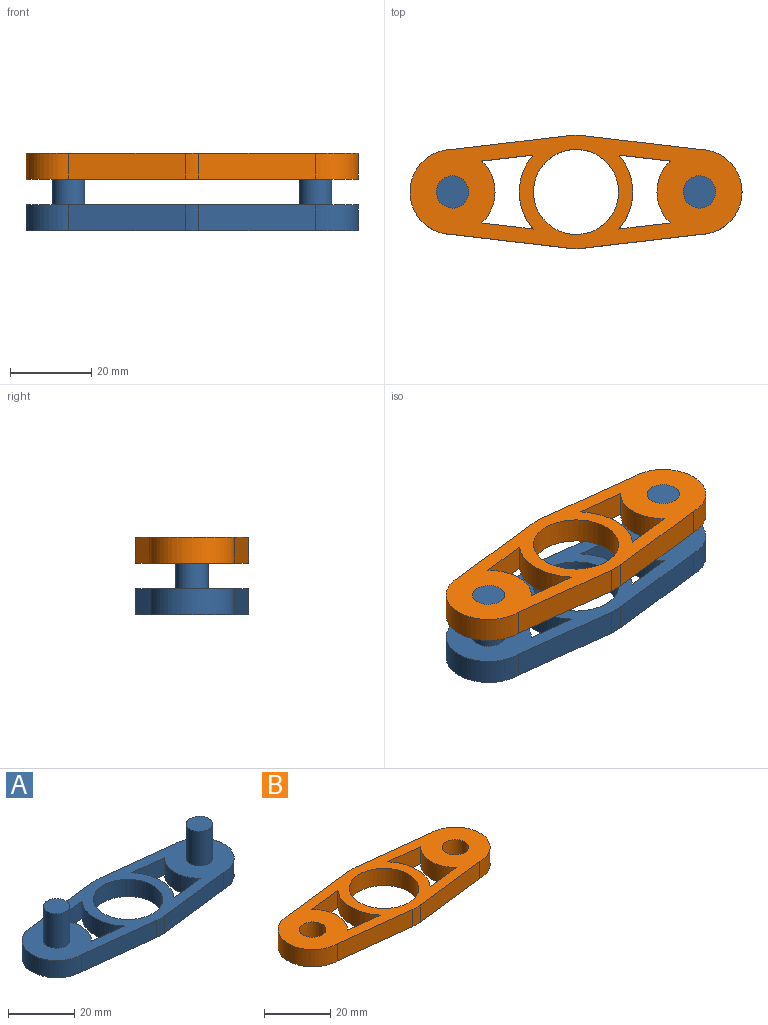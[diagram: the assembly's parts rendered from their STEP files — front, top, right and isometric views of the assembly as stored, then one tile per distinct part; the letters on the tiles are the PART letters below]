
ASSEMBLY  parts=2 mates=1
PART A: 23 faces, bbox 82x28x19.1 mm
  f0: plane 12.7x6.35mm, normal (-0.12,0.99,0), area 81.2mm2, adj f1,f14,f17,f18
  f1: cylinder r=14mm len=18.26mm, axis (0,0,-1), area 126.3mm2, adj f0,f2,f17,f18
  f2: plane 12.61x6.35mm, normal (-0.12,-0.99,0), area 80.6mm2, adj f1,f14,f17,f18
  f3: cylinder r=10.5mm len=15.27mm, axis (0,0,-1), area 108.6mm2, adj f4,f15,f17,f18
  f4: plane 12.61x6.35mm, normal (0.12,-0.99,0), area 80.6mm2, adj f3,f5,f17,f18
  f5: cylinder r=14mm len=18.26mm, axis (0,0,-1), area 126.3mm2, adj f4,f15,f17,f18
  f6: plane 28.84x6.35mm, normal (-0.12,0.99,0), area 184.4mm2, adj f7,f16,f17,f18
  f7: cylinder r=10.5mm len=21mm, axis (0,0,-1), area 209.5mm2, adj f6,f8,f17,f18
  f8: plane 28.84x6.35mm, normal (-0.12,-0.99,0), area 184.4mm2, adj f7,f9,f17,f18
  f9: cylinder r=14mm len=6.35mm, axis (0,0,-1), area 20.9mm2, adj f8,f10,f17,f18
  f10: plane 28.84x6.35mm, normal (0.12,-0.99,0), area 184.4mm2, adj f9,f11,f17,f18
  f11: cylinder r=10.5mm len=21mm, axis (0,0,-1), area 209.5mm2, adj f10,f12,f17,f18
  f12: plane 28.84x6.35mm, normal (0.12,0.99,0), area 184.4mm2, adj f11,f16,f17,f18
  f13: cylinder r=10.5mm len=21mm, axis (0,0,-1), area 418.9mm2, adj f17,f18
  f14: cylinder r=10.5mm len=15.27mm, axis (0,0,-1), area 108.6mm2, adj f0,f2,f17,f18
  f15: plane 12.7x6.35mm, normal (0.12,0.99,0), area 81.2mm2, adj f3,f5,f17,f18
  f16: cylinder r=14mm len=6.35mm, axis (0,0,-1), area 20.9mm2, adj f6,f12,f17,f18
  f17: plane 81.96x28mm, normal (0,0,1), area 1128.5mm2, adj f0,f1,f2,f3,f4,f5,f6,f7
  f18: plane 81.96x28mm, normal (0,0,-1), area 1229mm2, adj f0,f1,f2,f3,f4,f5,f6,f7
  f19: cylinder r=4mm len=12.7mm, axis (0,0,-1), area 319.2mm2, adj f17,f20
  f20: plane 8x8mm, normal (0,0,1), area 50.3mm2, adj f19
  f21: cylinder r=4mm len=12.7mm, axis (0,0,-1), area 319.2mm2, adj f17,f22
  f22: plane 8x8mm, normal (0,0,1), area 50.3mm2, adj f21
PART B: 21 faces, bbox 82x28x6.4 mm
  f0: plane 12.7x6.35mm, normal (-0.12,0.99,0), area 81.2mm2, adj f1,f14,f19,f20
  f1: cylinder r=14mm len=18.26mm, axis (0,0,-1), area 126.3mm2, adj f0,f2,f19,f20
  f2: plane 12.61x6.35mm, normal (-0.12,-0.99,0), area 80.6mm2, adj f1,f14,f19,f20
  f3: cylinder r=10.5mm len=15.27mm, axis (0,0,-1), area 108.6mm2, adj f4,f15,f19,f20
  f4: plane 12.61x6.35mm, normal (0.12,-0.99,0), area 80.6mm2, adj f3,f5,f19,f20
  f5: cylinder r=14mm len=18.26mm, axis (0,0,-1), area 126.3mm2, adj f4,f15,f19,f20
  f6: plane 28.84x6.35mm, normal (-0.12,0.99,0), area 184.4mm2, adj f7,f17,f19,f20
  f7: cylinder r=10.5mm len=21mm, axis (0,0,-1), area 209.5mm2, adj f6,f8,f19,f20
  f8: plane 28.84x6.35mm, normal (-0.12,-0.99,0), area 184.4mm2, adj f7,f9,f19,f20
  f9: cylinder r=14mm len=6.35mm, axis (0,0,-1), area 20.9mm2, adj f8,f10,f19,f20
  f10: plane 28.84x6.35mm, normal (0.12,-0.99,0), area 184.4mm2, adj f9,f11,f19,f20
  f11: cylinder r=10.5mm len=21mm, axis (0,0,-1), area 209.5mm2, adj f10,f12,f19,f20
  f12: plane 28.84x6.35mm, normal (0.12,0.99,0), area 184.4mm2, adj f11,f17,f19,f20
  f13: cylinder r=10.5mm len=21mm, axis (0,0,-1), area 418.9mm2, adj f19,f20
  f14: cylinder r=10.5mm len=15.27mm, axis (0,0,-1), area 108.6mm2, adj f0,f2,f19,f20
  f15: plane 12.7x6.35mm, normal (0.12,0.99,0), area 81.2mm2, adj f3,f5,f19,f20
  f16: cylinder r=4mm len=8mm, axis (0,0,-1), area 159.6mm2, adj f19,f20
  f17: cylinder r=14mm len=6.35mm, axis (0,0,-1), area 20.9mm2, adj f6,f12,f19,f20
  f18: cylinder r=4mm len=8mm, axis (0,0,-1), area 159.6mm2, adj f19,f20
  f19: plane 81.96x28mm, normal (0,0,1), area 1128.5mm2, adj f0,f1,f2,f3,f4,f5,f6,f7
  f20: plane 81.96x28mm, normal (0,0,-1), area 1128.5mm2, adj f0,f1,f2,f3,f4,f5,f6,f7
PLACE A at identity
PLACE B t=(0,0,15.88)mm
MATE fastened B.f3 <-> A.f3  axis (0,0,-1) through (-30.48,0,19.05)mm
